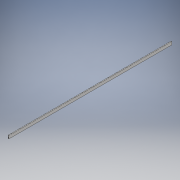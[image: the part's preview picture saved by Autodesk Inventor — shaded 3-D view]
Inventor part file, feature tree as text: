
AUTODESK INVENTOR PART (.ipt)
format: ipt  version: 2018 (Build 220112000, 112)  size: 115,200 bytes
history: native  units: mm
features: extrude x1, sketch x1
ambient origin geometry x8: Origin, YZ Plane, XZ Plane, XY Plane, X Axis, Y Axis, Z Axis, Center Point
bodies: Volumenkörper1 (feature_tree)
feature tree (2):
  extrude  "Extrusion1"  Depth=3.4mm
  sketch  "Skizze2"  dims[d0=1.0mm d1=3.4mm d2=0.3mm d3=0.5mm d4=0.5mm d5=197.5mm d6=0.0mm]
